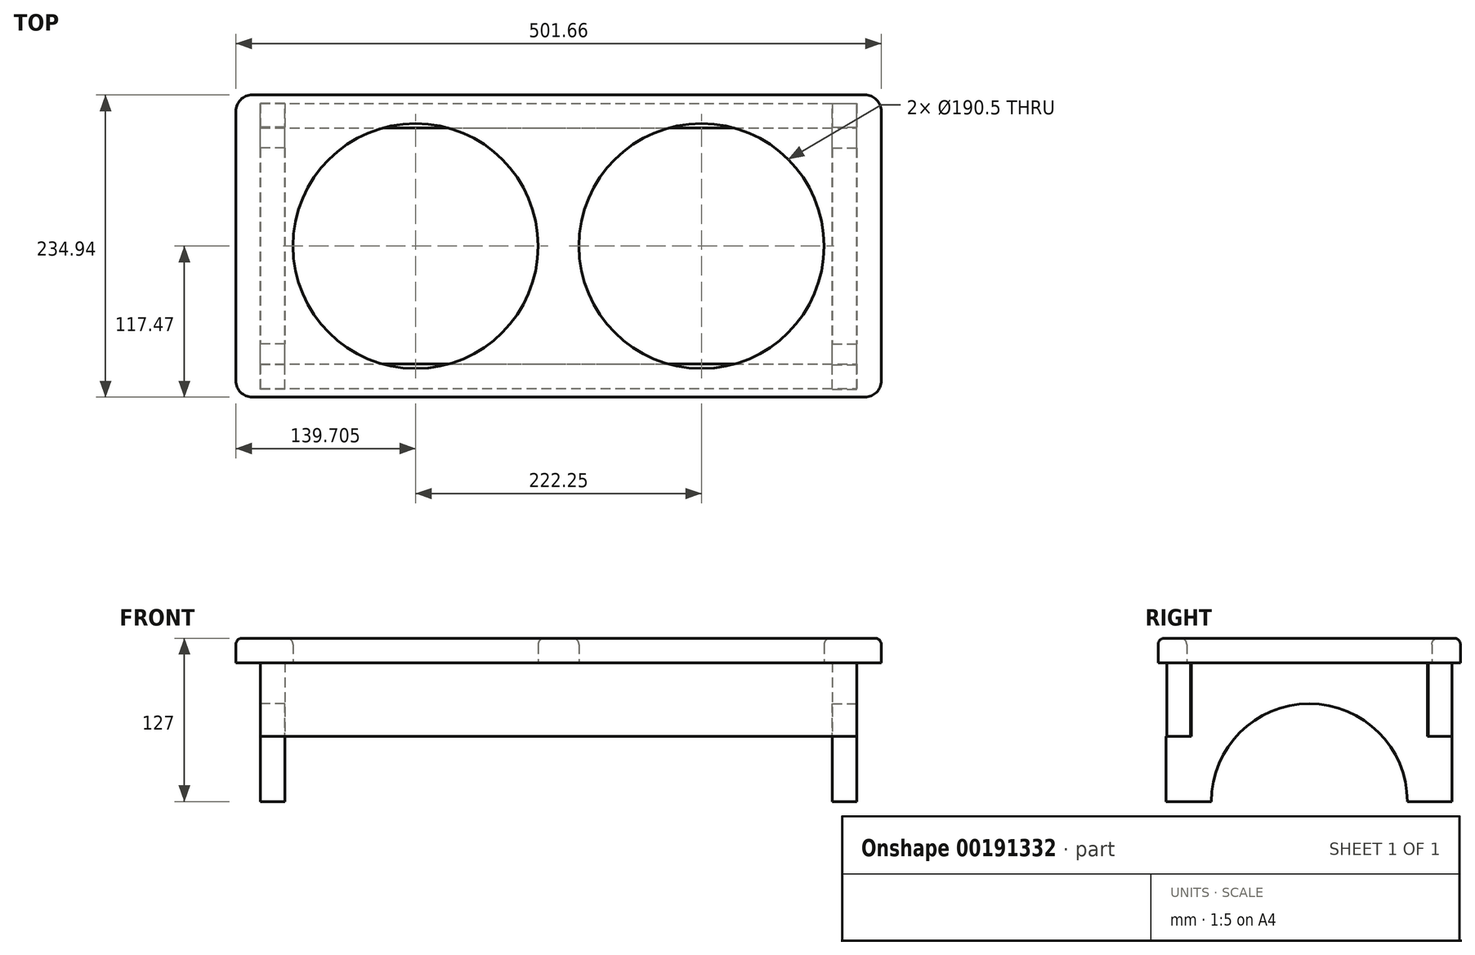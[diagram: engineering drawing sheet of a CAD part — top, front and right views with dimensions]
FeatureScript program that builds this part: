
annotation { "Feature Type Name" : "Feature", "Feature Type Description" : "" }
export const myFeature = defineFeature(function(context is Context, id is Id, definition is map)
    precondition{}
    {
        {
            var Q0;
            Q0=qCreatedBy(makeId("Top.planeOp"),FACE);
            var sketch = newSketch(context, id + "F0", { "sketchPlane" : qUnion([Q0])});
            skLineSegment(sketch, "E0.bottom", {"start": v(0, 117.48) * mm, "end": v(-238.13, 117.48) * mm});
            skLineSegment(sketch, "E0.top", {"start": v(0, -117.47) * mm, "end": v(-238.13, -117.48) * mm});
            skLineSegment(sketch, "E0.left", {"start": v(0, 117.48) * mm, "end": v(0, -117.47) * mm});
            skLineSegment(sketch, "E0.right", {"start": v(-250.83, 104.77) * mm, "end": v(-250.82, -104.77) * mm});
            skCircle(sketch, "E1", {"center": v(-238.13, 104.77) * mm, "radius": 12.7 * mm, "construction": true});
            skArc(sketch, "E2", {"start": v(-238.13, 117.47) * mm, "mid": v(-247.1, 113.76) * mm, "end": v(-250.83, 104.77) * mm});
            skArc(sketch, "E3.MirrorCS", {"start": v(-238.13, -117.47) * mm, "mid": v(-247.1, -113.76) * mm, "end": v(-250.83, -104.77) * mm});
            skCircle(sketch, "E4", {"center": v(-111.12, 0) * mm, "radius": 95.25 * mm});
            skLineSegment(sketch, "E5.MirrorCS", {"start": v(0, 117.48) * mm, "end": v(238.13, 117.48) * mm});
            skLineSegment(sketch, "E6.MirrorCS", {"start": v(250.83, 104.77) * mm, "end": v(250.82, -104.77) * mm});
            skLineSegment(sketch, "E7.MirrorCS", {"start": v(0, -117.47) * mm, "end": v(238.13, -117.48) * mm});
            skArc(sketch, "E8.MirrorCS", {"start": v(238.13, -117.48) * mm, "mid": v(247.1, -113.76) * mm, "end": v(250.83, -104.77) * mm});
            skArc(sketch, "E9.MirrorCS", {"start": v(238.13, 117.48) * mm, "mid": v(247.1, 113.76) * mm, "end": v(250.83, 104.77) * mm});
            skCircle(sketch, "E10.MirrorC", {"center": v(111.13, 0) * mm, "radius": 95.25 * mm});
            skSolve(sketch);
        }
        {
            var Q0;
            Q0=makeQuery(id+"F0.imprint","IMPRINT",FACE,{"disambiguationData":[TD([[makeQuery(id+"F0.imprint","IMPRINT",EDGE,{"derivedFrom":sQuery(id+"F0.wireOp",EDGE,"E0.bottom")}),1.0]])]});
            var Q1;
            Q1=makeQuery(id+"F0.imprint","IMPRINT",FACE,{"disambiguationData":[TD([[makeQuery(id+"F0.imprint","IMPRINT",EDGE,{"derivedFrom":sQuery(id+"F0.wireOp",EDGE,"E0.left")}),1.0]])]});
            extrude(context, id + "F1", {"entities" : qUnion([Q0, Q1]), "depth" : 19.05 * mm});
        }
        {
            var Q0;
            Q0=makeQuery(id+"F1.opExtrude","CAP_EDGE",EDGE,{"disambiguationData":[OSD([sQuery(id+"F0.wireOp",EDGE,"E0.top"),sQuery(id+"F0.wireOp",EDGE,"E7.MirrorCS")])],"isStart":false});
            var Q1;
            Q1=makeQuery(id+"F1.opExtrude","CAP_EDGE",EDGE,{"disambiguationData":[OSD([sQuery(id+"F0.wireOp",EDGE,"E4")])],"isStart":false});
            var Q2;
            Q2=makeQuery(id+"F1.opExtrude","CAP_EDGE",EDGE,{"disambiguationData":[OSD([sQuery(id+"F0.wireOp",EDGE,"E10.MirrorC")])],"isStart":false});
            fillet(context, id + "F2", {"entities" : qUnion([Q0, Q1, Q2]), "radius" : 4.76 * mm, "tangentPropagation" : true, "allowEdgeOverflow" : false});
        }
        {
            var Q0;
            Q0=qCreatedBy(makeId("Right.planeOp"),FACE);
            var sketch = newSketch(context, id + "F3", { "sketchPlane" : qUnion([Q0])});
            skLineSegment(sketch, "E11.bottom", {"start": v(-92.33, 0) * mm, "end": v(92.33, 0) * mm});
            skLineSegment(sketch, "E11.top", {"start": v(-111.38, -107.95) * mm, "end": v(-76.2, -107.95) * mm});
            skLineSegment(sketch, "E11.left", {"start": v(-111.38, -57.15) * mm, "end": v(-111.38, -107.95) * mm});
            skLineSegment(sketch, "E11.right", {"start": v(110.87, -57.15) * mm, "end": v(110.87, -107.95) * mm});
            skCircle(sketch, "E12", {"center": v(0, -107.95) * mm, "radius": 76.2 * mm, "construction": true});
            skArc(sketch, "E13", {"start": v(76.2, -107.95) * mm, "mid": v(0, -31.75) * mm, "end": v(-76.2, -107.95) * mm});
            skLineSegment(sketch, "E14.trimOffspring", {"start": v(76.2, -107.95) * mm, "end": v(110.87, -107.95) * mm});
            skLineSegment(sketch, "E15.top", {"start": v(-111.38, -57.15) * mm, "end": v(-92.33, -57.15) * mm});
            skLineSegment(sketch, "E15.right", {"start": v(-92.33, 0) * mm, "end": v(-92.33, -57.15) * mm});
            skPoint(sketch, "E16.orphan", {"position": v(-111.38, 0) * mm});
            skLineSegment(sketch, "E17", {"start": v(-140.04, 0) * mm, "end": v(178.22, 0) * mm, "construction": true});
            skLineSegment(sketch, "E18.MirrorCS", {"start": v(92.33, 0) * mm, "end": v(92.33, -57.15) * mm});
            skLineSegment(sketch, "E19.MirrorCS", {"start": v(111.38, -57.15) * mm, "end": v(92.33, -57.15) * mm});
            skSolve(sketch);
        }
        {
            var Q0;
            Q0=makeQuery(id+"F3.imprint","IMPRINT",FACE,{"disambiguationData":[TD([[makeQuery(id+"F3.imprint","IMPRINT",EDGE,{"derivedFrom":sQuery(id+"F3.wireOp",EDGE,"E11.bottom")}),-1.0]])]});
            extrude(context, id + "F4", {"entities" : qUnion([Q0]), "depth" : 19.05 * mm});
        }
        {
            var Q0;
            Q0=qCreatedBy(makeId("Front.planeOp"),FACE);
            var sketch = newSketch(context, id + "F5", { "sketchPlane" : qUnion([Q0])});
            skLineSegment(sketch, "E20.bottom", {"start": v(-231.78, 0) * mm, "end": v(231.78, 0) * mm});
            skLineSegment(sketch, "E20.top", {"start": v(-231.78, -57.15) * mm, "end": v(231.78, -57.15) * mm});
            skLineSegment(sketch, "E20.left", {"start": v(-231.78, 0) * mm, "end": v(-231.78, -57.15) * mm});
            skLineSegment(sketch, "E20.right", {"start": v(231.78, 0) * mm, "end": v(231.78, -57.15) * mm});
            skSolve(sketch);
        }
        {
            var Q0;
            {var subQ2=sQuery(id+"F5.wireOp",EDGE,"E20.left");Q0=makeQuery(id+"F5.imprint","IMPRINT",FACE,{"disambiguationData":[TD([[makeQuery(id+"F5.imprint","IMPRINT",EDGE,{"derivedFrom":subQ2}),1.0]])]});}
            var Q1;
            {var subQ2=sQuery(id+"F5.wireOp",EDGE,"E20.right");Q1=makeQuery(id+"F5.imprint","IMPRINT",FACE,{"disambiguationData":[TD([[makeQuery(id+"F5.imprint","IMPRINT",EDGE,{"derivedFrom":subQ2}),-1.0]])]});}
            var Q2;
            {var subQ1=sQuery(id+"F3.wireOp",EDGE,"E15.right");var subQ2=makeQuery(id+"F4.opExtrude","CAP_EDGE",EDGE,{"disambiguationData":[OSD([subQ1])],"isStart":true});Q2=makeQuery(id+"F5.imprint","IMPRINT",FACE,{"disambiguationData":[TD([[makeQuery(id+"F5.imprint","IMPRINT",EDGE,{"derivedFrom":subQ2}),1.0]])]});}
            extrude(context, id + "F6", {"entities" : qUnion([Q0, Q1, Q2]), "depth" : 19.05 * mm});
        }
        {
            var Q0;
            Q0=makeQuery(id+"F4.opExtrude","SWEPT_BODY",BODY,{"disambiguationData":[OSD([sQuery(id+"F3.wireOp",EDGE,"E11.bottom"),sQuery(id+"F3.wireOp",EDGE,"E11.top"),sQuery(id+"F3.wireOp",EDGE,"E11.left"),sQuery(id+"F3.wireOp",EDGE,"E11.right"),sQuery(id+"F3.wireOp",EDGE,"E13"),sQuery(id+"F3.wireOp",EDGE,"E14.trimOffspring"),sQuery(id+"F3.wireOp",EDGE,"E15.top"),sQuery(id+"F3.wireOp",EDGE,"E15.right"),sQuery(id+"F3.wireOp",EDGE,"E18.MirrorCS"),sQuery(id+"F3.wireOp",EDGE,"E19.MirrorCS")])]});
            transform(context, id + "F7", {"entities" : qUnion([Q0]), "transformType" : TransformType.TRANSLATION_3D, "dx" : -231.77 * mm, "dy" : 0 * mm, "dz" : 0 * mm, "makeCopy" : false});
        }
        {
            var Q0;
            Q0=makeQuery(id+"F4.opExtrude","SWEPT_BODY",BODY,{"disambiguationData":[OSD([sQuery(id+"F3.wireOp",EDGE,"E11.bottom"),sQuery(id+"F3.wireOp",EDGE,"E11.top"),sQuery(id+"F3.wireOp",EDGE,"E11.left"),sQuery(id+"F3.wireOp",EDGE,"E11.right"),sQuery(id+"F3.wireOp",EDGE,"E13"),sQuery(id+"F3.wireOp",EDGE,"E14.trimOffspring"),sQuery(id+"F3.wireOp",EDGE,"E15.top"),sQuery(id+"F3.wireOp",EDGE,"E15.right"),sQuery(id+"F3.wireOp",EDGE,"E18.MirrorCS"),sQuery(id+"F3.wireOp",EDGE,"E19.MirrorCS")])]});
            var Q1;
            Q1=qCreatedBy(makeId("Right.planeOp"),FACE);
            mirror(context, id + "F8", {"entities" : qUnion([Q0]), "mirrorPlane" : qUnion([Q1])});
        }
        {
            var Q0;
            Q0=makeQuery(id+"F6.opExtrude","SWEPT_BODY",BODY,{"disambiguationData":[OSD([sQuery(id+"F5.wireOp",EDGE,"E20.bottom"),sQuery(id+"F5.wireOp",EDGE,"E20.top"),sQuery(id+"F5.wireOp",EDGE,"E20.left"),sQuery(id+"F5.wireOp",EDGE,"E20.right")])]});
            transform(context, id + "F9", {"entities" : qUnion([Q0]), "transformType" : TransformType.TRANSLATION_3D, "dx" : 0 * mm, "dy" : 110.87 * mm, "dz" : 0 * mm, "makeCopy" : false});
        }
        {
            var Q0;
            Q0=makeQuery(id+"F6.opExtrude","SWEPT_BODY",BODY,{"disambiguationData":[OSD([sQuery(id+"F5.wireOp",EDGE,"E20.bottom"),sQuery(id+"F5.wireOp",EDGE,"E20.top"),sQuery(id+"F5.wireOp",EDGE,"E20.left"),sQuery(id+"F5.wireOp",EDGE,"E20.right")])]});
            var Q1;
            Q1=qCreatedBy(makeId("Front.planeOp"),FACE);
            mirror(context, id + "F10", {"entities" : qUnion([Q0]), "mirrorPlane" : qUnion([Q1])});
        }
    });
